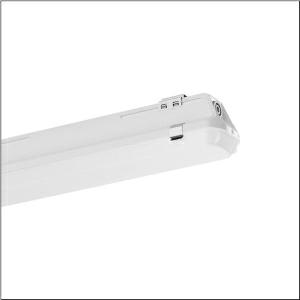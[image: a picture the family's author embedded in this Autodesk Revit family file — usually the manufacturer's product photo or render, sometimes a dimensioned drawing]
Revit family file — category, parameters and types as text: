
# Revit family: monsun_r__11_facade_51ff40mp460h_34d2
name_source: partatom
category: Lighting Fixtures
units: mm (PartAtom-declared; Revit-internal decimal feet)

## family parameters
Cut with Voids When Loaded = No
Host = Face
Light Source = No
Part Type = Normal
Room Calculation Point = No
Round Connector Dimension = Use Diameter
Shared = No

## types (1)
- --- (1 x LED, 6110 lm, 33.5 W, 4000K)
    Apparent Load = 34 VA
    CIE Flux Codes = 47 77 93 95 100
    Color Rendering = 80
    Color Temperature = 4000K
    Default Elevation = 1800 mm
    Description = Monsun® 11 facade, damp-proof luminaire, chain hanger, primary optical cover: enclosure, of PMMA, light emission: direct distribution, primary light characteristic: symmetric, installation type: surface-mounted, horizontal mounting, vertical mounting, LED, rated luminous flux: 6.110lm, luminous efficacy: 182lm/W, light colour: 840, colour temperature: 4000K, control gear: ECG, with terminal, 3-pole, max. 2.5mm², mains connection: 220..240V, AC, 50/60Hz, rated input power: 34W, luminaire housing, of glass-fibre reinforced polyester, uncoated, bright grey, incl. chain hanger, for cables, Ø 8.4..12mm, with climate membrane, length: 1.590mm, width: 90mm, height: 88mm, clip for enclosure, of stainless steel (V2A), ceiling mounting element, of stainless steel (V2A), chain hanger, of stainless steel (V2A), protection rating (complete): IP66, insulation class (complete): insulation class I (protective earthing), certification: CE, ENEC, VDE, UKCA, protection symbol: D, impact resistance: IK06, permissible operating ambient temperature: -35..+50°C, standard: EN 50419, EN 60598-2-1, contact your sales advisor before using the luminaires in applications with unclear chemical exposure, large temperature fluctuations or condensation-forming humidity, LABS conformity tested according to VDMA 24364:2018-05, exposed outdoor area, packaging unit: 1 piece
    Height = 89 mm
    Lamp = 1 x LED
    Lamp Light Flux = 6110 lm
    Lamp Power = 33.5 W
    Lamp count = 1
    Length = 1590 mm
    Luminous efficacy = 182 lm/W
    Manufacturer = Siteco
    ModVariant = No
    Model = 51FF40MP460H
    Mounting Place = Ceiling
    Mounting Type = Surface mounted
    Number of Poles = 1
    OnlyDefault = Yes
    Power Factor = 1
    Product Name = Monsun® 11 facade
    Product group = damp-proof luminaire
    ProductGroupID = 300
    Protection Class = Protection class I
    Protection Degree = IP 66
    RLX_Detail_Level = 1
    RLX_Emergency_Light_Flux = 0 lm
    RLX_Emergency_Type = 0
    RLX_Emergency_Type_DB = No
    RlxData = <blob elided: 89605 chars, md5=55a495cc>
    Socket = socket
    Standby Power = 0 W
    System Light Flux = 6110 lm
    System Power = 34 W
    Type Comments = factory setting: luminous flux: 100 % | (A | C | E) | 77 mA
    Type Image = l_1004748.jpg
    URL = http://relux.com
    VarID = @adj_142001
    Voltage = 0 V
    Weight = 0.00 kg
    Width = 90 mm

## geometry (parser evidence)
native form markers: Blend x4, Sweep x12
no freeform markers — native parametric forms only
